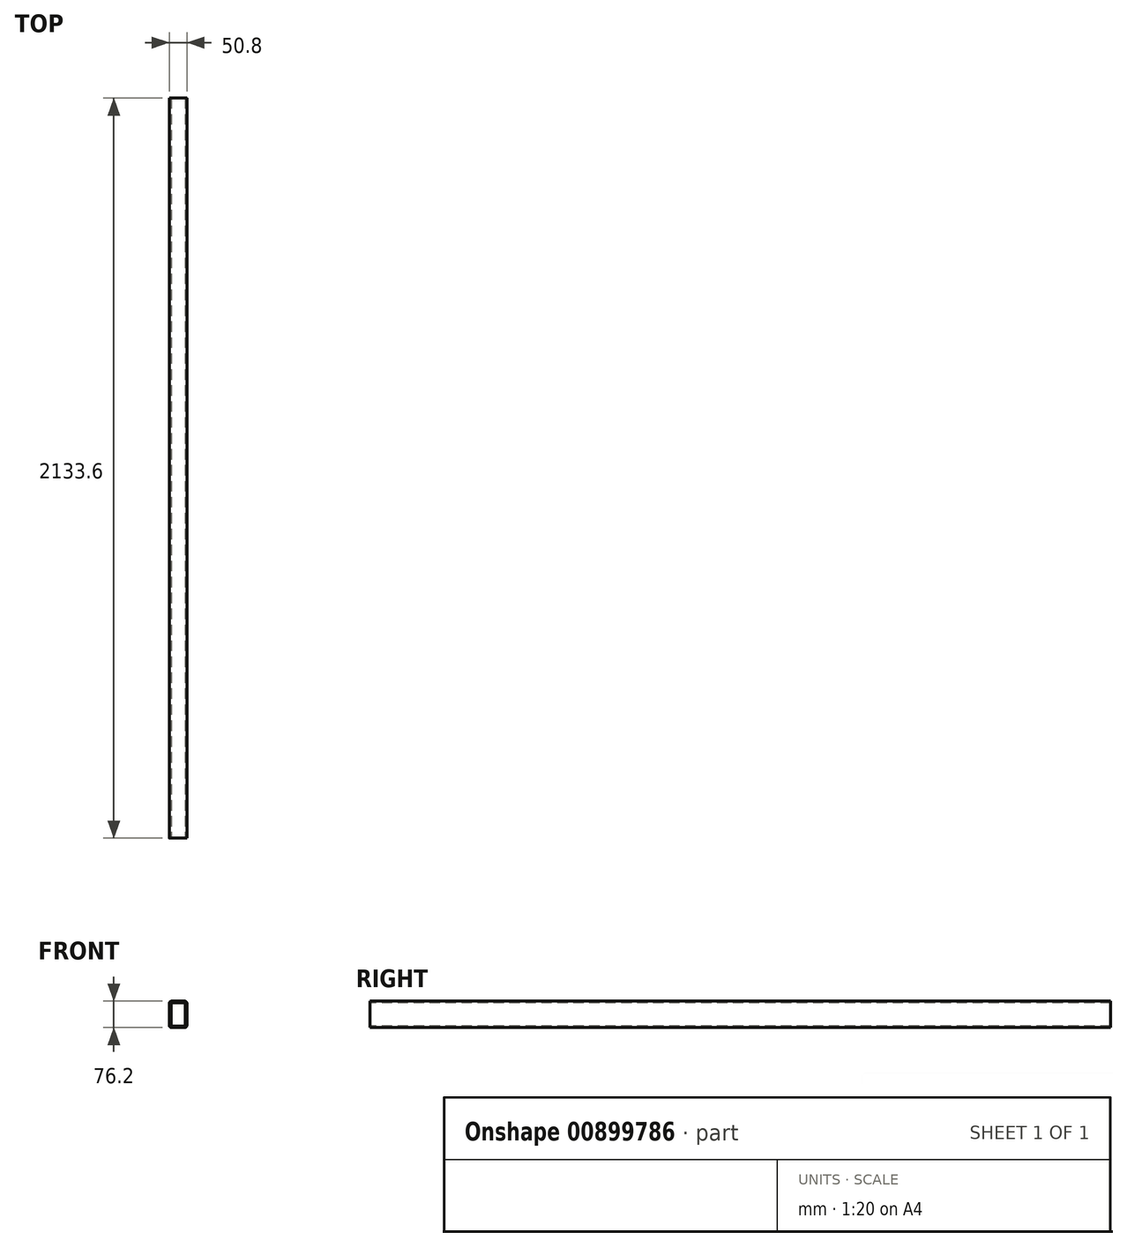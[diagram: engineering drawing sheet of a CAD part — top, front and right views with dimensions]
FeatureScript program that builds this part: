
annotation { "Feature Type Name" : "Feature", "Feature Type Description" : "" }
export const myFeature = defineFeature(function(context is Context, id is Id, definition is map)
    precondition{}
    {
        {
            var Q0;
            Q0=qCreatedBy(makeId("Front.planeOp"),FACE);
            var sketch = newSketch(context, id + "F0", { "sketchPlane" : qUnion([Q0])});
            skLineSegment(sketch, "E0.bottom", {"start": v(19.05, 38.1) * mm, "end": v(-19.05, 38.1) * mm});
            skLineSegment(sketch, "E0.top", {"start": v(19.05, -38.1) * mm, "end": v(-19.05, -38.1) * mm});
            skLineSegment(sketch, "E0.left", {"start": v(25.4, 31.75) * mm, "end": v(25.4, -31.75) * mm});
            skLineSegment(sketch, "E0.right", {"start": v(-25.4, 31.75) * mm, "end": v(-25.4, -31.75) * mm});
            skPoint(sketch, "E0.middle", {"position": v(0, 0) * mm});
            skPoint(sketch, "E1.visualSharp", {"position": v(-25.4, 38.1) * mm});
            skArc(sketch, "E1.filletArc", {"start": v(-19.05, 38.1) * mm, "mid": v(-23.54, 36.24) * mm, "end": v(-25.4, 31.75) * mm});
            skPoint(sketch, "E2.visualSharp", {"position": v(25.4, 38.1) * mm});
            skArc(sketch, "E2.filletArc", {"start": v(25.4, 31.75) * mm, "mid": v(23.54, 36.24) * mm, "end": v(19.05, 38.1) * mm});
            skPoint(sketch, "E3.visualSharp", {"position": v(25.4, -38.1) * mm});
            skArc(sketch, "E3.filletArc", {"start": v(19.05, -38.1) * mm, "mid": v(23.54, -36.24) * mm, "end": v(25.4, -31.75) * mm});
            skPoint(sketch, "E4.visualSharp", {"position": v(-25.4, -38.1) * mm});
            skArc(sketch, "E4.filletArc", {"start": v(-25.4, -31.75) * mm, "mid": v(-23.54, -36.24) * mm, "end": v(-19.05, -38.1) * mm});
            skArc(sketch, "E5.0", {"start": v(20.62, 31.75) * mm, "mid": v(20.16, 32.86) * mm, "end": v(19.05, 33.32) * mm});
            skLineSegment(sketch, "E5.1", {"start": v(20.62, 31.75) * mm, "end": v(20.62, -31.75) * mm});
            skLineSegment(sketch, "E5.2", {"start": v(19.05, 33.32) * mm, "end": v(-19.05, 33.32) * mm});
            skArc(sketch, "E5.3", {"start": v(19.05, -33.32) * mm, "mid": v(20.16, -32.86) * mm, "end": v(20.62, -31.75) * mm});
            skArc(sketch, "E5.4", {"start": v(-19.05, 33.32) * mm, "mid": v(-20.16, 32.86) * mm, "end": v(-20.62, 31.75) * mm});
            skLineSegment(sketch, "E5.5", {"start": v(-20.62, 31.75) * mm, "end": v(-20.62, -31.75) * mm});
            skArc(sketch, "E5.6", {"start": v(-20.62, -31.75) * mm, "mid": v(-20.16, -32.86) * mm, "end": v(-19.05, -33.32) * mm});
            skLineSegment(sketch, "E5.7", {"start": v(19.05, -33.32) * mm, "end": v(-19.05, -33.32) * mm});
            skSolve(sketch);
        }
        {
            var Q0;
            Q0 = qSketchRegion(id + "F0", true);
            var Q1;
            Q1=sQuery(id+"F0.wireOp",EDGE,"E0.right");
            var Q2;
            Q2=sQuery(id+"F0.wireOp",EDGE,"E1.filletArc");
            var Q3;
            Q3=sQuery(id+"F0.wireOp",EDGE,"E0.bottom");
            var Q4;
            Q4=sQuery(id+"F0.wireOp",EDGE,"E2.filletArc");
            var Q5;
            Q5=sQuery(id+"F0.wireOp",EDGE,"E0.left");
            var Q6;
            Q6=sQuery(id+"F0.wireOp",EDGE,"E3.filletArc");
            var Q7;
            Q7=sQuery(id+"F0.wireOp",EDGE,"E0.top");
            var Q8;
            Q8=sQuery(id+"F0.wireOp",EDGE,"E4.filletArc");
            var Q9;
            Q9=sQuery(id+"F0.wireOp",EDGE,"E5.7");
            var Q10;
            Q10=sQuery(id+"F0.wireOp",EDGE,"E5.6");
            var Q11;
            Q11=sQuery(id+"F0.wireOp",EDGE,"E5.5");
            var Q12;
            Q12=sQuery(id+"F0.wireOp",EDGE,"E5.4");
            var Q13;
            Q13=sQuery(id+"F0.wireOp",EDGE,"E5.2");
            var Q14;
            Q14=sQuery(id+"F0.wireOp",EDGE,"E5.0");
            var Q15;
            Q15=sQuery(id+"F0.wireOp",EDGE,"E5.1");
            var Q16;
            Q16=sQuery(id+"F0.wireOp",EDGE,"E5.3");
            extrude(context, id + "F1", {"entities" : qUnion([Q0]), "bodyType" : ToolBodyType.SURFACE, "surfaceEntities" : qUnion([Q1, Q2, Q3, Q4, Q5, Q6, Q7, Q8, Q9, Q10, Q11, Q12, Q13, Q14, Q15, Q16]), "depth" : 2133.6 * mm, "offsetDistance" : 25.4 * mm});
        }
    });
